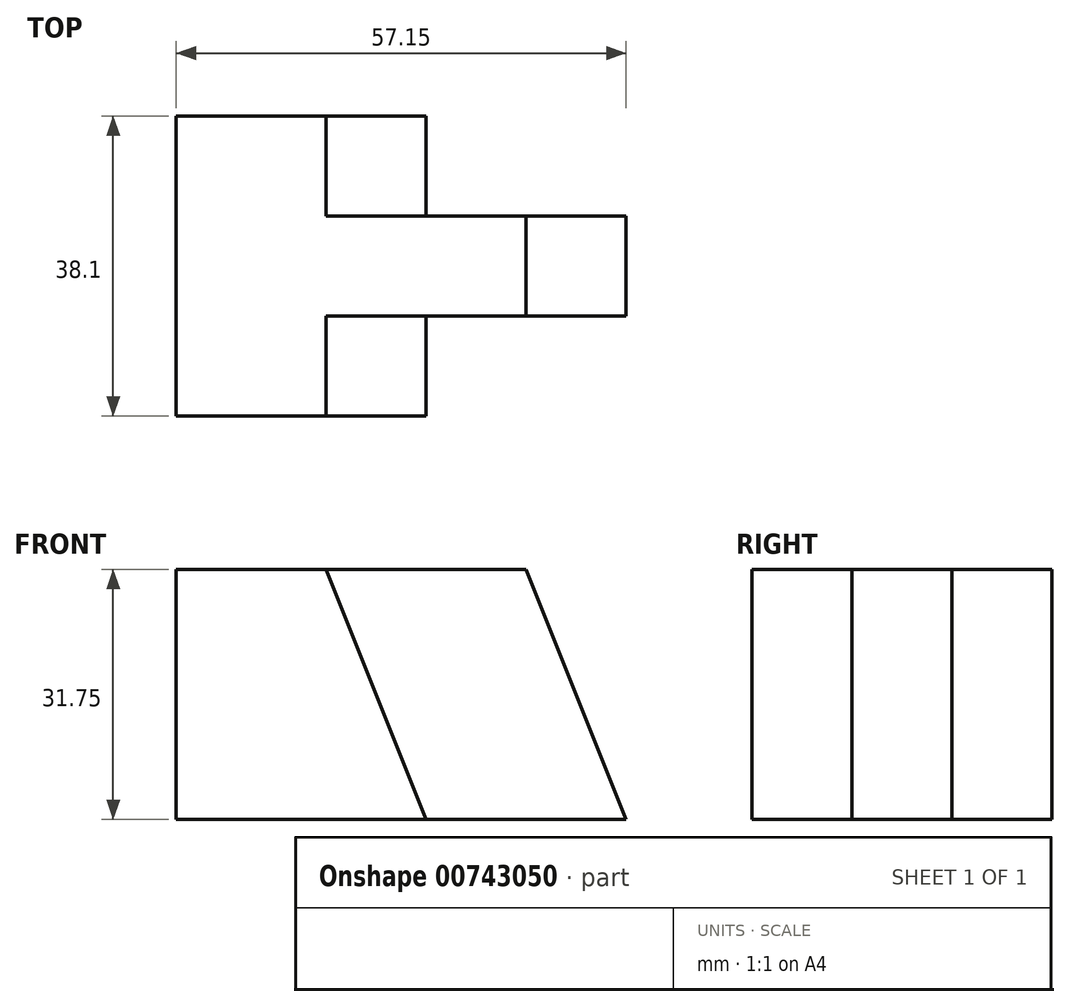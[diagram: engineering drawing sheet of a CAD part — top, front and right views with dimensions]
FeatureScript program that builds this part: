
annotation { "Feature Type Name" : "Feature", "Feature Type Description" : "" }
export const myFeature = defineFeature(function(context is Context, id is Id, definition is map)
    precondition{}
    {
        {
            var Q0;
            Q0=qCreatedBy(makeId("Front.planeOp"),FACE);
            var sketch = newSketch(context, id + "F0", { "sketchPlane" : qUnion([Q0])});
            skLineSegment(sketch, "E0", {"start": v(0, 0) * mm, "end": v(31.75, 0) * mm});
            skLineSegment(sketch, "E1", {"start": v(31.75, 0) * mm, "end": v(31.75, 31.75) * mm});
            skLineSegment(sketch, "E2", {"start": v(31.75, 31.75) * mm, "end": v(0, 31.75) * mm});
            skLineSegment(sketch, "E3", {"start": v(0, 31.75) * mm, "end": v(0, 0) * mm});
            skSolve(sketch);
        }
        {
            var Q0;
            Q0=makeQuery(id+"F0.imprint","IMPRINT",FACE,{"disambiguationData":[TD([[makeQuery(id+"F0.imprint","IMPRINT",EDGE,{"derivedFrom":sQuery(id+"F0.wireOp",EDGE,"E0")}),1.0]])]});
            extrude(context, id + "F1", {"entities" : qUnion([Q0]), "oppositeDirection" : true, "depth" : 38.1 * mm, "offsetDistance" : 25.4 * mm});
        }
        {
            var Q0;
            Q0=makeQuery(id+"F1.opExtrude","CAP_FACE",FACE,{"disambiguationData":[OSD([sQuery(id+"F0.wireOp",EDGE,"E0"),sQuery(id+"F0.wireOp",EDGE,"E1"),sQuery(id+"F0.wireOp",EDGE,"E2"),sQuery(id+"F0.wireOp",EDGE,"E3")])],"isStart":true});
            var sketch = newSketch(context, id + "F2", { "sketchPlane" : qUnion([Q0])});
            skLineSegment(sketch, "E4", {"start": v(19.05, 31.75) * mm, "end": v(31.75, 0) * mm});
            skLineSegment(sketch, "E5", {"start": v(31.75, 0) * mm, "end": v(31.75, 31.75) * mm});
            skSolve(sketch);
        }
        {
            var Q0;
            Q0 = qSketchRegion(id + "F2", true);
            var Q1;
            {var subQ0=sQuery(id+"F2.wireOp",EDGE,"E4");Q1=makeQuery(id+"F2.imprint","IMPRINT",FACE,{"disambiguationData":[TD([[makeQuery(id+"F2.imprint","IMPRINT",EDGE,{"derivedFrom":subQ0}),1.0]])]});}
            extrude(context, id + "F3", {"entities" : qUnion([Q0, Q1]), "operationType" : NewBodyOperationType.REMOVE, "oppositeDirection" : true, "depth" : 12.7 * mm, "offsetDistance" : 25.4 * mm});
        }
        {
            var Q0;
            Q0=makeQuery(id+"F1.opExtrude","CAP_FACE",FACE,{"disambiguationData":[OSD([sQuery(id+"F0.wireOp",EDGE,"E0"),sQuery(id+"F0.wireOp",EDGE,"E1"),sQuery(id+"F0.wireOp",EDGE,"E2"),sQuery(id+"F0.wireOp",EDGE,"E3")])],"isStart":false});
            var sketch = newSketch(context, id + "F4", { "sketchPlane" : qUnion([Q0])});
            skLineSegment(sketch, "E6", {"start": v(-19.05, 31.75) * mm, "end": v(-31.75, 0) * mm});
            skLineSegment(sketch, "E7", {"start": v(-31.75, 0) * mm, "end": v(-31.75, 31.75) * mm});
            skLineSegment(sketch, "E8", {"start": v(-31.75, 31.75) * mm, "end": v(-19.05, 31.75) * mm});
            skSolve(sketch);
        }
        {
            var Q0;
            Q0 = qSketchRegion(id + "F4", true);
            extrude(context, id + "F5", {"entities" : qUnion([Q0]), "operationType" : NewBodyOperationType.REMOVE, "oppositeDirection" : true, "depth" : 12.7 * mm, "offsetDistance" : 25.4 * mm});
        }
        {
            var Q0;
            Q0=makeQuery(id+"F1.opExtrude","SWEPT_FACE",FACE,{"disambiguationData":[OSD([sQuery(id+"F0.wireOp",EDGE,"E1")])]});
            extrude(context, id + "F6", {"entities" : qUnion([Q0]), "operationType" : NewBodyOperationType.ADD, "depth" : 25.4 * mm, "offsetDistance" : 25.4 * mm});
        }
        {
            var Q0;
            {var subQ0=sQuery(id+"F2.wireOp",EDGE,"E5");Q0=makeQuery(id+"F6.boolean.opBoolean","MERGE",FACE,{"derivedFrom":[makeQuery(id+"F3.boolean.opBoolean","COPY",FACE,{"derivedFrom":makeQuery(id+"F3.opExtrude","CAP_FACE",FACE,{"disambiguationData":[OSD([sQuery(id+"F0.wireOp",EDGE,"E2"),sQuery(id+"F2.wireOp",EDGE,"E4"),subQ0])],"isStart":false})}),makeQuery(id+"F6.opExtrude","SWEPT_FACE",FACE,{"disambiguationData":[OSD([subQ0])]})]});}
            var sketch = newSketch(context, id + "F7", { "sketchPlane" : qUnion([Q0])});
            skLineSegment(sketch, "E9", {"start": v(57.15, 31.75) * mm, "end": v(44.45, 31.75) * mm});
            skLineSegment(sketch, "E10", {"start": v(44.45, 31.75) * mm, "end": v(57.15, 0) * mm});
            skLineSegment(sketch, "E11", {"start": v(57.15, 0) * mm, "end": v(57.15, 31.75) * mm});
            skSolve(sketch);
        }
        {
            var Q0;
            Q0=makeQuery(id+"F7.imprint","IMPRINT",FACE,{"disambiguationData":[TD([[makeQuery(id+"F7.imprint","IMPRINT",EDGE,{"derivedFrom":sQuery(id+"F7.wireOp",EDGE,"E9")}),1.0]])]});
            extrude(context, id + "F8", {"entities" : qUnion([Q0]), "operationType" : NewBodyOperationType.REMOVE, "oppositeDirection" : true, "depth" : 12.7 * mm, "offsetDistance" : 25.4 * mm});
        }
    });
